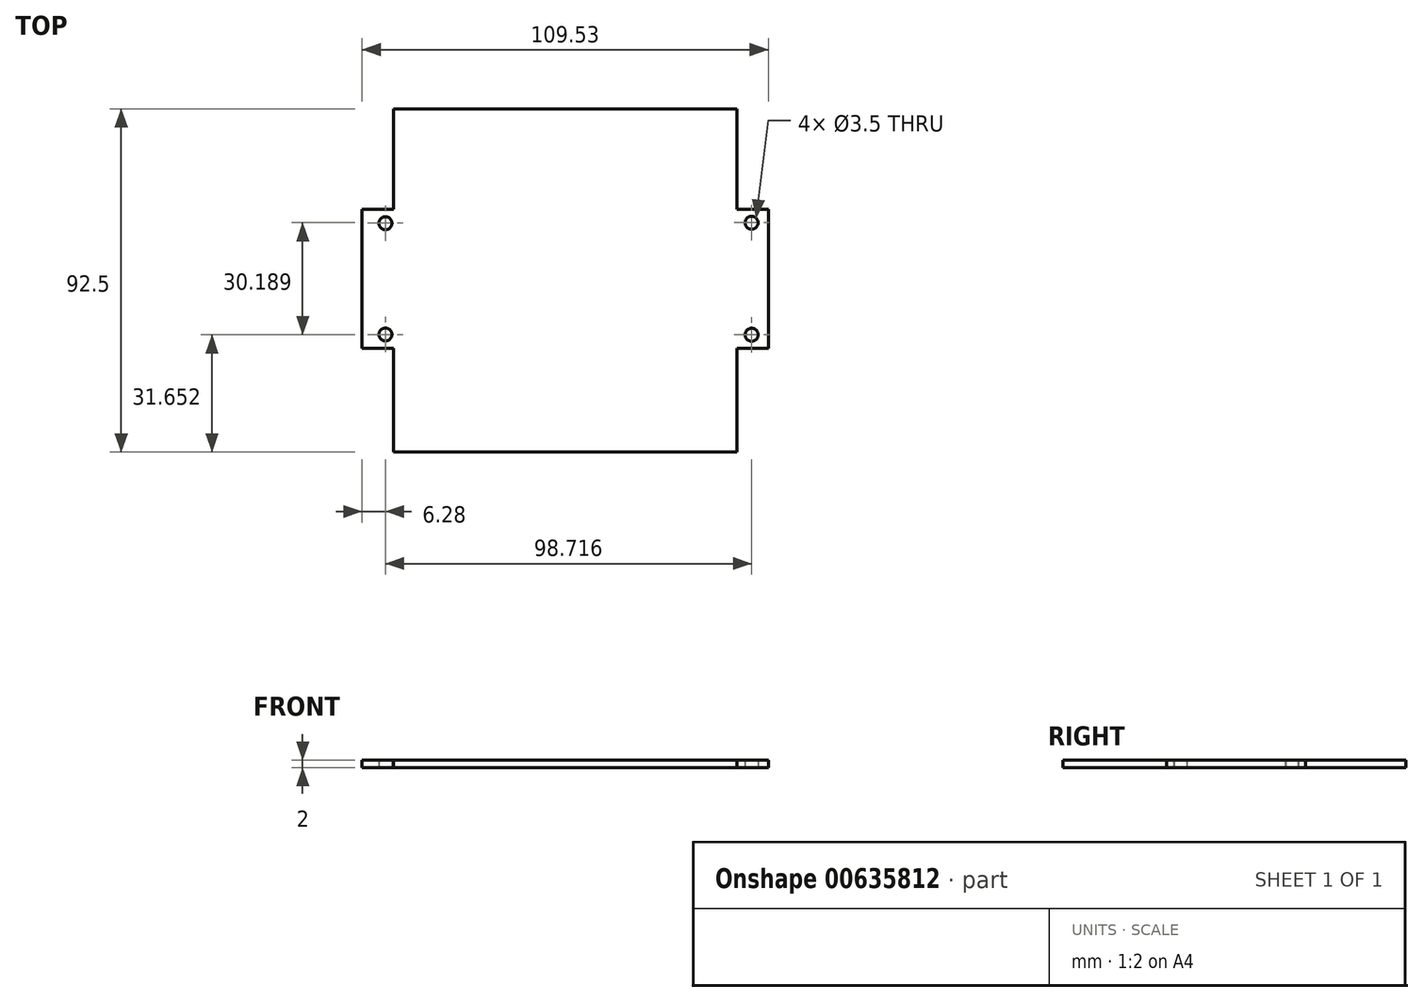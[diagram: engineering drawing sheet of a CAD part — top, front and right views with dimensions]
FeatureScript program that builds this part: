
annotation { "Feature Type Name" : "Feature", "Feature Type Description" : "" }
export const myFeature = defineFeature(function(context is Context, id is Id, definition is map)
    precondition{}
    {
        {
            var Q0;
            Q0=qCreatedBy(makeId("Top.planeOp"),FACE);
            var sketch = newSketch(context, id + "F0", { "sketchPlane" : qUnion([Q0])});
            skLineSegment(sketch, "E0.bottom", {"start": v(-34.72, 69.56) * mm, "end": v(57.78, 69.56) * mm});
            skLineSegment(sketch, "E0.top", {"start": v(-34.72, -22.94) * mm, "end": v(57.78, -22.94) * mm});
            skPoint(sketch, "E1", {"position": v(-34.72, 42.56) * mm});
            skPoint(sketch, "E2", {"position": v(-34.72, 5.06) * mm});
            skPoint(sketch, "E3", {"position": v(57.78, 42.56) * mm});
            skPoint(sketch, "E4", {"position": v(57.78, 5.06) * mm});
            skLineSegment(sketch, "E5", {"start": v(57.78, 42.56) * mm, "end": v(66.3, 42.56) * mm});
            skLineSegment(sketch, "E6", {"start": v(66.3, 42.56) * mm, "end": v(66.3, 5.06) * mm});
            skLineSegment(sketch, "E7", {"start": v(66.3, 5.06) * mm, "end": v(57.78, 5.06) * mm});
            skLineSegment(sketch, "E8", {"start": v(-34.72, 42.56) * mm, "end": v(-43.22, 42.56) * mm});
            skLineSegment(sketch, "E9", {"start": v(-43.22, 42.56) * mm, "end": v(-43.22, 5.06) * mm});
            skLineSegment(sketch, "E10", {"start": v(-43.22, 5.06) * mm, "end": v(-34.72, 5.06) * mm});
            skCircle(sketch, "E11", {"center": v(-36.94, 38.78) * mm, "radius": 1.75 * mm});
            skCircle(sketch, "E12", {"center": v(61.78, 8.71) * mm, "radius": 1.75 * mm});
            skCircle(sketch, "E13", {"center": v(-36.94, 8.78) * mm, "radius": 1.75 * mm});
            skLineSegment(sketch, "E14", {"start": v(-34.72, 42.56) * mm, "end": v(-34.72, 69.56) * mm});
            skLineSegment(sketch, "E15", {"start": v(-34.72, 5.06) * mm, "end": v(-34.72, -22.94) * mm});
            skLineSegment(sketch, "E16", {"start": v(57.78, 42.56) * mm, "end": v(57.78, 69.56) * mm});
            skLineSegment(sketch, "E17", {"start": v(57.78, 5.06) * mm, "end": v(57.78, -22.94) * mm});
            skLineSegment(sketch, "E18", {"start": v(61.78, 5.06) * mm, "end": v(61.78, 8.71) * mm});
            skLineSegment(sketch, "E19", {"start": v(61.78, 8.71) * mm, "end": v(66.3, 8.71) * mm});
            skCircle(sketch, "E20", {"center": v(61.77, 38.9) * mm, "radius": 1.75 * mm});
            skSolve(sketch);
        }
        {
            var Q0;
            Q0=qSketchRegion(id+"F0",true);
            extrude(context, id + "F1", {"entities" : qUnion([Q0]), "depth" : 2 * mm, "offsetDistance" : 25 * mm});
        }
    });
